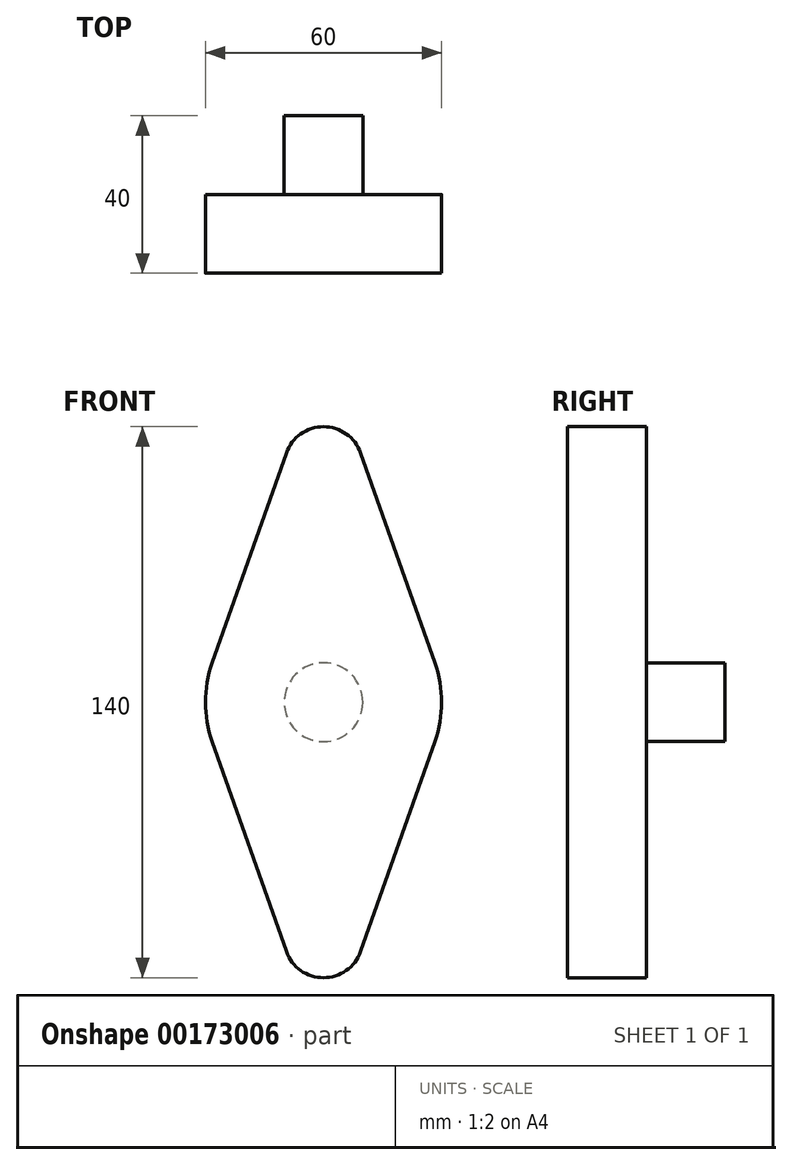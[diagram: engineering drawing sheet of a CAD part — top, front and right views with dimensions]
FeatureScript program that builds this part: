
annotation { "Feature Type Name" : "Feature", "Feature Type Description" : "" }
export const myFeature = defineFeature(function(context is Context, id is Id, definition is map)
    precondition{}
    {
        {
            var Q0;
            Q0=qCreatedBy(makeId("Front.planeOp"),FACE);
            var sketch = newSketch(context, id + "F0", { "sketchPlane" : qUnion([Q0])});
            skCircle(sketch, "E0", {"center": v(0, 0) * mm, "radius": 30 * mm});
            skCircle(sketch, "E1", {"center": v(0, 60) * mm, "radius": 10 * mm});
            skCircle(sketch, "E2", {"center": v(0, -60) * mm, "radius": 10 * mm});
            skLineSegment(sketch, "E3", {"start": v(0, 60) * mm, "end": v(0, -60) * mm, "construction": true});
            skLineSegment(sketch, "E4", {"start": v(-9.43, 63.33) * mm, "end": v(-28.28, 10) * mm});
            skLineSegment(sketch, "E5.MirrorCS", {"start": v(9.43, 63.33) * mm, "end": v(28.28, 10) * mm});
            skLineSegment(sketch, "E6", {"start": v(-28.28, -10) * mm, "end": v(-9.43, -63.33) * mm});
            skLineSegment(sketch, "E7.MirrorCS", {"start": v(28.28, -10) * mm, "end": v(9.43, -63.33) * mm});
            skSolve(sketch);
        }
        {
            var Q0;
            Q0 = qSketchRegion(id + "F0", true);
            extrude(context, id + "F1", {"entities" : qUnion([Q0]), "depth" : 20 * mm});
        }
        {
            var Q0;
            Q0=makeQuery(id+"F1.opExtrude","CAP_FACE",FACE,{"disambiguationData":[OSD([sQuery(id+"F0.wireOp",EDGE,"E0"),sQuery(id+"F0.wireOp",EDGE,"E1"),sQuery(id+"F0.wireOp",EDGE,"E2"),sQuery(id+"F0.wireOp",EDGE,"E4"),sQuery(id+"F0.wireOp",EDGE,"E5.MirrorCS"),sQuery(id+"F0.wireOp",EDGE,"E6"),sQuery(id+"F0.wireOp",EDGE,"E7.MirrorCS")])],"isStart":true});
            var sketch = newSketch(context, id + "F2", { "sketchPlane" : qUnion([Q0])});
            skCircle(sketch, "E8", {"center": v(0, 0) * mm, "radius": 10 * mm});
            skSolve(sketch);
        }
        {
            var Q0;
            Q0 = qSketchRegion(id + "F2", true);
            extrude(context, id + "F3", {"entities" : qUnion([Q0]), "operationType" : NewBodyOperationType.ADD, "depth" : 20 * mm});
        }
    });
